# Revit family: VNRBH - 2-5-Door - All
name_source: partatom
category: Mechanical Equipment
units: mm (PartAtom-declared; Revit-internal decimal feet)

## family parameters
Always vertical = Yes
Cut with Voids When Loaded = No
OmniClass Number = 23.40.40.11.17
OmniClass Title = Refrigerated Cases
Part Type = Normal
Room Calculation Point = No
Round Connector Dimension = Use Radius
Shared = No
Work Plane-Based = Yes

## types (11) — shared parameters
24" Shelf = Yes
Certifications = NSF 7, UL471, CSA
DATE = 02/08/2016
DISCHARGE AIR TEMP. = -1 °F
DISCHARGE AIR VELOCITY = 0 FPM
DRAIN LINE CONNECTION = SANITARY LINE CONNECTION
DRAIN LINE DIAMETER = 2"
DRAIN PIPE TYPE = PVC
DRIP PAN PLUMB TYPE = HARD
Default Elevation = 48"
Defrost Num Day = 2
Defrost Termination = 42 °F
Defrost Type = TIMED-OFF DEFROST
Defrosts Per Day_2 = 2
Description = Narrow Reach-In Merchandiser
Discharge Air Velocity (FPM) = 360 (FPM)
EQUIPMENT DESCRIPTION = Narrow Reach-In Merchandiser
EQUIPMENT MARK = VNRBH
GLASS = Glass
Height = 89 7/8"
Item Description = Narrow Reach-In Merchandiser
Keynote = VNRBH
LIQUID LINE CONNECTION = LIQUID LINE CONNECTION
LIQUID LINE DIAMETER = 0"
LIQUID LINE RADIUS = 0"
Legend Number = VNRBH
Manufacturer = HILL PHOENIX
Model = VNRBH
PAINTED METAL UPPER SHELF = PAINTED SHELVES
PRESSURE REGULATOR = 0.00 psi
REFRIGERATION PIPING = COPPER PIPE
Refrig Charge Lbs = 0
SANITARY PIPE SIZE = 1"
STAINLESS STEEL = GALVANIZED STEEL
SUCTION LINE CONNECTION = SUCTION LINE CONNECTION
SUCTION LINE DIAMETER = 1"
SUCTION LINE RADIUS = 0"
Superheat Set Point @ Bulb (°F) = 6-8° F
TIMED OFF DEFROST FAIL-SAFE (Min) = 30
TIMED OFF DEFROST TERMINATION TEMP = 38 °F
Timed-Off Defrost Fail-Safe (Min) = 30 (Min)
Timed-Off Defrost Termination Temp_2 = 42° F
URL = http://www.hillphoenix.com
Width = 37 1/8"
vista c amps = 0 A
zero-valued in all types: Evap Temp, Load Mbh

## per-type parameters (varying)
- 2-Door - Beverage: Application Discipline=Beverage; BTUH Conventional=720; BTUH Parallel=716; CENTER LINE & DRAIN=30"; Discharge Air (°F)=38° F; Evaporator (°F)=34° F; GE Gen6 Amps=0 A; GE Gen6 Watts=33 W; High Efficiency Amps=0 A; High Efficiency Watts=52 W; Infinity 90 Amps=0 A; Infinity 90 Watts=44 W; LEDStixx Amps=0 A; LEDStixx Watts=52 W; Length=60"; Length of Cases=60"; NUMBER FOR GUIDLINES AND CONTROL ORGANIZATION=0; NUMBER FOR LIGHTING DATA=1; NUMBER OF DOORS=2; Number of Fans=2; Pro24 35K Hi Output Amps=0 A; Pro24 35K Hi Output Watts=36 W; Size of Doors=30"; Type of Door Swing=B-Swing; VISTA E AMPS=1 A; VISTA E WATTS=149 W; Vista-C Amps=0 A; Vista-C Watts=44 W; Vista-C/60 Amps=1 A; Vista-C/60 Watts=75 W
- 3-Door - Beverage: Application Discipline=Beverage/Produce; BTUH Conventional=625; BTUH Parallel=620; CENTER LINE & DRAIN=45"; Discharge Air (°F)=39° F; Evaporator (°F)=34° F; GE Gen6 Amps=0 A; GE Gen6 Watts=51 W; High Efficiency Amps=1 A; High Efficiency Watts=78 W; Infinity 90 Amps=1 A; Infinity 90 Watts=70 W; LEDStixx Amps=1 A; LEDStixx Watts=74 W; Length=90"; Length of Cases=90"; NUMBER FOR GUIDLINES AND CONTROL ORGANIZATION=1; NUMBER FOR LIGHTING DATA=2; NUMBER OF DOORS=3; Number of Fans=3; Pro24 35K Hi Output Amps=1 A; Pro24 35K Hi Output Watts=54 W; Size of Doors=30"; Type of Door Swing=A-Swing; VISTA E AMPS=2 A; VISTA E WATTS=206 W; Vista-C Amps=1 A; Vista-C Watts=70 W; Vista-C/60 Amps=1 A; Vista-C/60 Watts=103 W
- 4-Door - Beverage: Application Discipline=Beverage; BTUH Conventional=720; BTUH Parallel=716; CENTER LINE & DRAIN=60"; Discharge Air (°F)=38° F; Evaporator (°F)=34° F; GE Gen6 Amps=1 A; GE Gen6 Watts=68 W; High Efficiency Amps=1 A; High Efficiency Watts=104 W; Infinity 90 Amps=1 A; Infinity 90 Watts=97 W; LEDStixx Amps=1 A; LEDStixx Watts=96 W; Length=120"; Length of Cases=120"; NUMBER FOR GUIDLINES AND CONTROL ORGANIZATION=0; NUMBER FOR LIGHTING DATA=3; NUMBER OF DOORS=4; Number of Fans=4; Pro24 35K Hi Output Amps=1 A; Pro24 35K Hi Output Watts=72 W; Size of Doors=30"; Type of Door Swing=B-Swing; VISTA E AMPS=2 A; VISTA E WATTS=253 W; Vista-C Amps=1 A; Vista-C Watts=97 W; Vista-C/60 Amps=1 A; Vista-C/60 Watts=127 W
- 5-Door - Beverage: Application Discipline=Beverage; BTUH Conventional=720; BTUH Parallel=716; CENTER LINE & DRAIN=75"; Discharge Air (°F)=38° F; Evaporator (°F)=34° F; GE Gen6 Amps=1 A; GE Gen6 Watts=86 W; High Efficiency Amps=1 A; High Efficiency Watts=130 W; Infinity 90 Amps=1 A; Infinity 90 Watts=122 W; LEDStixx Amps=1 A; LEDStixx Watts=118 W; Length=150"; Length of Cases=150"; NUMBER FOR GUIDLINES AND CONTROL ORGANIZATION=0; NUMBER FOR LIGHTING DATA=4; NUMBER OF DOORS=5; Number of Fans=5; Pro24 35K Hi Output Amps=1 A; Pro24 35K Hi Output Watts=89 W; Size of Doors=30"; Type of Door Swing=A-Swing; VISTA E AMPS=3 A; VISTA E WATTS=303 W; Vista-C Amps=1 A; Vista-C Watts=122 W; Vista-C/60 Amps=1 A; Vista-C/60 Watts=152 W
- 12' 24" Doors Beverage: Application Discipline=Beverage/Produce; BTUH Conventional=500; BTUH Parallel=495; CENTER LINE & DRAIN=72"; Discharge Air (°F)=39° F; Evaporator (°F)=34° F; GE Gen6 Amps=0 A; GE Gen6 Watts=48 W; High Efficiency Amps=1 A; High Efficiency Watts=78 W; Infinity 90 Amps=1 A; Infinity 90 Watts=85 W; LEDStixx Amps=1 A; LEDStixx Watts=74 W; Length=144"; Length of Cases=144"; NUMBER FOR GUIDLINES AND CONTROL ORGANIZATION=15; NUMBER FOR LIGHTING DATA=11; NUMBER OF DOORS=5; Number of Fans=3; Pro24 35K Hi Output Amps=0 A; Pro24 35K Hi Output Watts=54 W; Size of Doors=24"; Type of Door Swing=A-Swing; VISTA E AMPS=2 A; VISTA E WATTS=225 W; Vista-C Amps=1 A; Vista-C Watts=85 W; Vista-C/60 Amps=1 A; Vista-C/60 Watts=124 W
- 8' 32" Doors Beverage: Application Discipline=Beverage/Produce; BTUH Conventional=665; BTUH Parallel=660; CENTER LINE & DRAIN=48"; Discharge Air (°F)=39° F; Evaporator (°F)=34° F; GE Gen6 Amps=0 A; GE Gen6 Watts=51 W; High Efficiency Amps=0 A; High Efficiency Watts=52 W; Infinity 90 Amps=1 A; Infinity 90 Watts=71 W; LEDStixx Amps=1 A; LEDStixx Watts=74 W; Length=96"; Length of Cases=96"; NUMBER FOR GUIDLINES AND CONTROL ORGANIZATION=14; NUMBER FOR LIGHTING DATA=10; NUMBER OF DOORS=5; Number of Fans=2; Pro24 35K Hi Output Amps=0 A; Pro24 35K Hi Output Watts=54 W; Size of Doors=32"; Type of Door Swing=A-Swing; VISTA E AMPS=2 A; VISTA E WATTS=180 W; Vista-C Amps=1 A; Vista-C Watts=71 W; Vista-C/60 Amps=1 A; Vista-C/60 Watts=90 W
- 12' 36" Doors Beverage: Application Discipline=Beverage/Produce; BTUH Conventional=750; BTUH Parallel=745; CENTER LINE & DRAIN=72"; Discharge Air (°F)=39° F; Evaporator (°F)=34° F; GE Gen6 Amps=1 A; GE Gen6 Watts=68 W; High Efficiency Amps=1 A; High Efficiency Watts=78 W; Infinity 90 Amps=1 A; Infinity 90 Watts=103 W; LEDStixx Amps=1 A; LEDStixx Watts=96 W; Length=144"; Length of Cases=144"; NUMBER FOR GUIDLINES AND CONTROL ORGANIZATION=16; NUMBER FOR LIGHTING DATA=12; NUMBER OF DOORS=5; Number of Fans=3; Pro24 35K Hi Output Amps=1 A; Pro24 35K Hi Output Watts=72 W; Size of Doors=36"; Type of Door Swing=A-Swing; VISTA E AMPS=2 A; VISTA E WATTS=225 W; Vista-C Amps=1 A; Vista-C Watts=103 W; Vista-C/60 Amps=1 A; Vista-C/60 Watts=113 W
- 4' 24" Doors Deli: Application Discipline=Deli/Dairy/Cut Produce; BTUH Conventional=555; BTUH Parallel=550; CENTER LINE & DRAIN=24"; Discharge Air (°F)=35 °F; Evaporator (°F)=31° F; GE Gen6 Amps=0 A; GE Gen6 Watts=18 W; High Efficiency Amps=0 A; High Efficiency Watts=26 W; Infinity 90 Amps=0 A; Infinity 90 Watts=23 W; LEDStixx Amps=0 A; LEDStixx Watts=37 W; Length=48"; Length of Cases=48"; NUMBER FOR GUIDLINES AND CONTROL ORGANIZATION=18; NUMBER FOR LIGHTING DATA=5; NUMBER OF DOORS=5; Number of Fans=1; Pro24 35K Hi Output Amps=0 A; Pro24 35K Hi Output Watts=19 W; Size of Doors=24"; Type of Door Swing=A-Swing; VISTA E AMPS=1 A; VISTA E WATTS=113 W; Vista-C Amps=0 A; Vista-C Watts=23 W; Vista-C/60 Amps=0 A; Vista-C/60 Watts=57 W
- 8' 24" Doors Deli: Application Discipline=Deli/Dairy/Cut Produce; BTUH Conventional=555; BTUH Parallel=550; CENTER LINE & DRAIN=48"; Discharge Air (°F)=35 °F; Evaporator (°F)=31° F; GE Gen6 Amps=0 A; GE Gen6 Watts=33 W; High Efficiency Amps=0 A; High Efficiency Watts=52 W; Infinity 90 Amps=0 A; Infinity 90 Watts=53 W; LEDStixx Amps=0 A; LEDStixx Watts=52 W; Length=96"; Length of Cases=96"; NUMBER FOR GUIDLINES AND CONTROL ORGANIZATION=20; NUMBER FOR LIGHTING DATA=9; NUMBER OF DOORS=5; Number of Fans=2; Pro24 35K Hi Output Amps=0 A; Pro24 35K Hi Output Watts=36 W; Size of Doors=24"; Type of Door Swing=A-Swing; VISTA E AMPS=2 A; VISTA E WATTS=181 W; Vista-C Amps=0 A; Vista-C Watts=53 W; Vista-C/60 Amps=2 A; Vista-C/60 Watts=181 W
- 8' 32" Doors Dei: Application Discipline=Deli/Dairy/Cut Produce; BTUH Conventional=740; BTUH Parallel=730; CENTER LINE & DRAIN=48"; Discharge Air (°F)=35 °F; Evaporator (°F)=31° F; GE Gen6 Amps=0 A; GE Gen6 Watts=51 W; High Efficiency Amps=0 A; High Efficiency Watts=52 W; Infinity 90 Amps=1 A; Infinity 90 Watts=155 W; LEDStixx Amps=1 A; LEDStixx Watts=74 W; Length=96"; Length of Cases=96"; NUMBER FOR GUIDLINES AND CONTROL ORGANIZATION=21; NUMBER FOR LIGHTING DATA=0; NUMBER OF DOORS=5; Number of Fans=2; Pro24 35K Hi Output Amps=0 A; Pro24 35K Hi Output Watts=54 W; Size of Doors=32"; Type of Door Swing=A-Swing; VISTA E AMPS=2 A; VISTA E WATTS=180 W; Vista-C Amps=2 A; Vista-C Watts=180 W; Vista-C/60 Amps=2 A; Vista-C/60 Watts=180 W
- 6' 24" Doors: Application Discipline=Deli/Dairy/Cut Produce; BTUH Conventional=555; BTUH Parallel=550; CENTER LINE & DRAIN=36"; Discharge Air (°F)=35 °F; Evaporator (°F)=31° F; GE Gen6 Amps=0 A; GE Gen6 Watts=18 W; High Efficiency Amps=0 A; High Efficiency Watts=52 W; Infinity 90 Amps=0 A; Infinity 90 Watts=48 W; LEDStixx Amps=0 A; LEDStixx Watts=37 W; Length=72"; Length of Cases=72"; NUMBER FOR GUIDLINES AND CONTROL ORGANIZATION=18; NUMBER FOR LIGHTING DATA=5; NUMBER OF DOORS=5; Number of Fans=2; Pro24 35K Hi Output Amps=0 A; Pro24 35K Hi Output Watts=19 W; Size of Doors=24"; Type of Door Swing=A-Swing; VISTA E AMPS=1 A; VISTA E WATTS=113 W; Vista-C Amps=0 A; Vista-C Watts=48 W; Vista-C/60 Amps=0 A; Vista-C/60 Watts=57 W

## geometry (parser evidence)
native form markers: Blend x12, Sweep x17
no freeform markers — native parametric forms only
